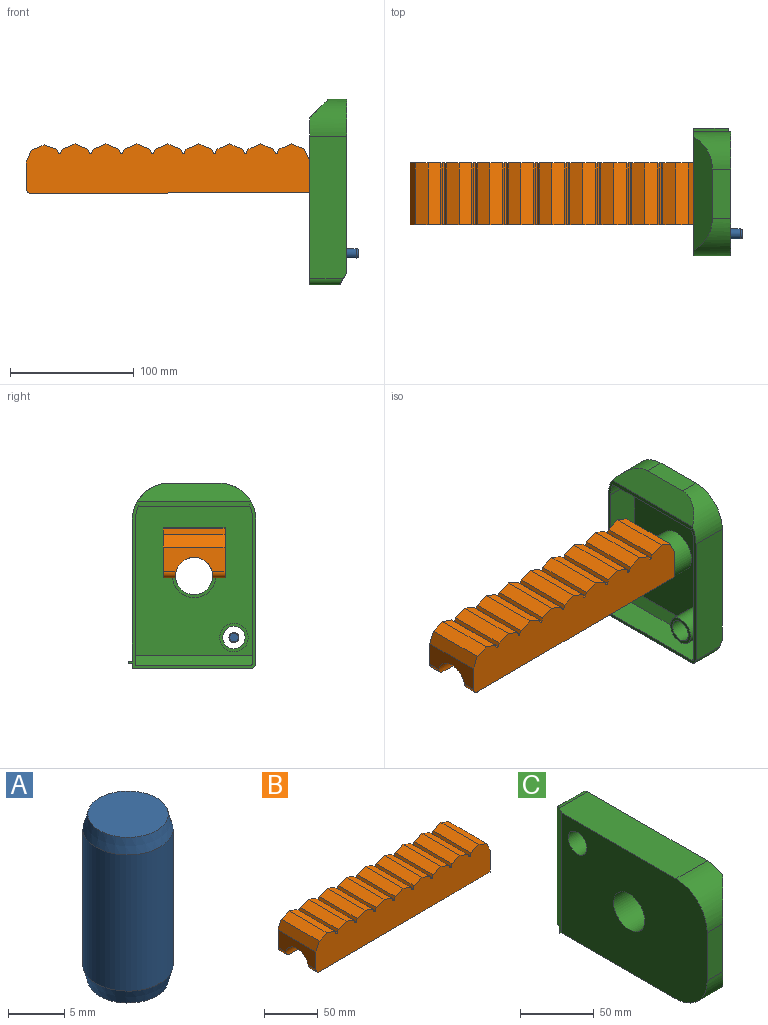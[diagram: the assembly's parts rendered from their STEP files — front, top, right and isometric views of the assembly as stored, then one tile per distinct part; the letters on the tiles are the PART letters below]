
ASSEMBLY  parts=3 mates=2
PART A: 5 faces, bbox 8x8x18 mm
  f0: plane 7.14x7.14mm, normal (0,0,1), area 40.1mm2, adj f1
  f1: cone r=3.57mm half-angle=15deg, axis (0,0,-1), area 39.4mm2, adj f0,f2
  f2: cylinder r=4mm len=14.8mm, axis (0,0,-1), area 372mm2, adj f1,f3
  f3: cone r=4mm half-angle=15deg, axis (0,0,1), area 39.4mm2, adj f2,f4
  f4: plane 7.14x7.14mm, normal (0,0,-1), area 40.1mm2, adj f3
PART B: 53 faces, bbox 229.3x50x40.4 mm
  f0: plane 50x19.96mm, normal (-1,0,0), area 746.4mm2, adj f1,f21,f22,f50,f51,f52
  f1: cylinder r=5mm len=10.39mm, axis (0,1,0), area 79.5mm2, adj f0,f2,f50,f52
  f2: plane 224.25x10.08mm, normal (0.01,0,-1), area 2248.8mm2, adj f1,f23,f50,f52
  f3: plane 224.25x10.08mm, normal (0.01,0,-1), area 2248.8mm2, adj f22,f23,f51,f52
  f4: plane 50x10.36mm, normal (0.38,0,0.92), area 560.4mm2, adj f5,f49,f50,f51
  f5: plane 50x10.36mm, normal (-0.38,0,0.92), area 560.4mm2, adj f4,f6,f50,f51
  f6: plane 50x2.95mm, normal (-0.92,0,0.38), area 159.5mm2, adj f5,f7,f50,f51
  f7: cylinder r=1mm len=50mm, axis (0,1,0), area 117.8mm2, adj f6,f8,f50,f51
  f8: plane 50x2.95mm, normal (0.92,0,0.38), area 159.5mm2, adj f7,f9,f50,f51
  f9: plane 50x10.36mm, normal (0.38,0,0.92), area 560.4mm2, adj f8,f10,f50,f51
  f10: plane 50x10.36mm, normal (-0.38,0,0.92), area 560.4mm2, adj f9,f11,f50,f51
  f11: plane 50x2.95mm, normal (-0.92,0,0.38), area 159.5mm2, adj f10,f12,f50,f51
  f12: cylinder r=1mm len=50mm, axis (0,1,0), area 117.8mm2, adj f11,f13,f50,f51
  f13: plane 50x2.95mm, normal (0.92,0,0.38), area 159.5mm2, adj f12,f14,f50,f51
  f14: plane 50x10.36mm, normal (0.38,0,0.92), area 560.4mm2, adj f13,f15,f50,f51
  f15: plane 50x10.36mm, normal (-0.38,0,0.92), area 560.4mm2, adj f14,f16,f50,f51
  f16: plane 50x2.95mm, normal (-0.92,0,0.38), area 159.5mm2, adj f15,f17,f50,f51
  f17: cylinder r=1mm len=50mm, axis (0,1,0), area 117.8mm2, adj f16,f18,f50,f51
  f18: plane 50x2.95mm, normal (0.92,0,0.38), area 159.5mm2, adj f17,f19,f50,f51
  f19: plane 50x10.36mm, normal (0.32,0,0.95), area 546.7mm2, adj f18,f20,f50,f51
  f20: plane 50x10.36mm, normal (-0.38,0,0.92), area 560.4mm2, adj f19,f21,f50,f51
  f21: plane 50x10.36mm, normal (-0.92,0,0.38), area 560.4mm2, adj f0,f20,f50,f51
  f22: cylinder r=5mm len=10.39mm, axis (0,1,0), area 79.5mm2, adj f0,f3,f51,f52
  f23: plane 50x25mm, normal (1,0,0), area 896.6mm2, adj f2,f3,f24,f50,f51,f52
  f24: plane 50x9.52mm, normal (0.91,0,0.41), area 522.1mm2, adj f23,f25,f50,f51
  f25: plane 50x10.36mm, normal (0.38,0,0.92), area 560.4mm2, adj f24,f26,f50,f51
  f26: plane 50x10.36mm, normal (-0.38,0,0.92), area 560.4mm2, adj f25,f27,f50,f51
  f27: plane 50x2.95mm, normal (-0.92,0,0.38), area 159.5mm2, adj f26,f28,f50,f51
  f28: cylinder r=1mm len=50mm, axis (0,1,0), area 117.8mm2, adj f27,f29,f50,f51
  f29: plane 50x2.95mm, normal (0.92,0,0.38), area 159.5mm2, adj f28,f30,f50,f51
  f30: plane 50x10.36mm, normal (0.38,0,0.92), area 560.4mm2, adj f29,f31,f50,f51
  f31: plane 50x10.36mm, normal (-0.38,0,0.92), area 560.4mm2, adj f30,f32,f50,f51
  f32: plane 50x2.95mm, normal (-0.92,0,0.38), area 159.5mm2, adj f31,f33,f50,f51
  f33: cylinder r=1mm len=50mm, axis (0,1,0), area 117.8mm2, adj f32,f34,f50,f51
  f34: plane 50x2.95mm, normal (0.92,0,0.38), area 159.5mm2, adj f33,f35,f50,f51
  f35: plane 50x10.36mm, normal (0.38,0,0.92), area 560.4mm2, adj f34,f36,f50,f51
  f36: plane 50x10.36mm, normal (-0.38,0,0.92), area 560.4mm2, adj f35,f37,f50,f51
  f37: plane 50x2.95mm, normal (-0.92,0,0.38), area 159.5mm2, adj f36,f38,f50,f51
  f38: cylinder r=1mm len=50mm, axis (0,1,0), area 117.8mm2, adj f37,f39,f50,f51
  f39: plane 50x2.95mm, normal (0.92,0,0.38), area 159.5mm2, adj f38,f40,f50,f51
  f40: plane 50x10.36mm, normal (0.38,0,0.92), area 560.4mm2, adj f39,f41,f50,f51
  f41: plane 50x10.36mm, normal (-0.38,0,0.92), area 560.4mm2, adj f40,f42,f50,f51
  f42: plane 50x2.95mm, normal (-0.92,0,0.38), area 159.5mm2, adj f41,f43,f50,f51
  f43: cylinder r=1mm len=50mm, axis (0,1,0), area 117.8mm2, adj f42,f44,f50,f51
  f44: plane 50x2.95mm, normal (0.92,0,0.38), area 159.5mm2, adj f43,f45,f50,f51
  f45: plane 50x10.36mm, normal (0.38,0,0.92), area 560.4mm2, adj f44,f46,f50,f51
  f46: plane 50x10.36mm, normal (-0.38,0,0.92), area 560.4mm2, adj f45,f47,f50,f51
  f47: plane 50x2.95mm, normal (-0.92,0,0.38), area 159.5mm2, adj f46,f48,f50,f51
  f48: cylinder r=1mm len=50mm, axis (0,1,0), area 117.8mm2, adj f47,f49,f50,f51
  f49: plane 50x2.95mm, normal (0.92,0,0.38), area 159.5mm2, adj f4,f48,f50,f51
  f50: plane 229.29x40.39mm, normal (0,-1,0), area 8357.7mm2, adj f0,f1,f2,f4,f5,f6,f7,f8
  f51: plane 229.29x40.39mm, normal (0,1,0), area 8357.7mm2, adj f0,f3,f4,f5,f6,f7,f8,f9
  f52: cylinder r=15mm len=229.29mm, axis (1,0,0), area 11165.5mm2, adj f0,f1,f2,f3,f22,f23
PART C: 31 faces, bbox 30x150x103.4 mm
  f0: plane 135x103.37mm, normal (1,0,0), area 1231.3mm2, adj f3,f4,f5,f6,f8,f9,f11,f14
  f1: plane 23.1x23.1mm, normal (1,0,0), area 161.8mm2, adj f10,f23
  f2: plane 35x35mm, normal (1,0,0), area 255.3mm2, adj f12,f24
  f3: plane 26.59x3.37mm, normal (0,1,0), area 89.7mm2, adj f0,f4,f11,f17
  f4: plane 26.59x4.09mm, normal (0,0,-1), area 103.9mm2, adj f0,f3,f5,f17
  f5: plane 95x24.23mm, normal (0,1,0), area 2301.5mm2, adj f0,f4,f17,f18
  f6: plane 115x30mm, normal (0,0,1), area 3442.8mm2, adj f0,f13,f14,f17,f18
  f7: plane 40x15mm, normal (0,-1,0), area 600mm2, adj f13,f14,f15,f16
  f8: plane 113.77x30mm, normal (0,0,-1), area 3409mm2, adj f0,f9,f13,f15,f17
  f9: plane 27.82x3.37mm, normal (0,-1,0), area 93.8mm2, adj f0,f8,f11,f17
  f10: cylinder r=9.05mm len=30mm, axis (-1,0,0), area 1705.9mm2, adj f1,f13
  f11: plane 27.82x2.14mm, normal (0,0,-1), area 58.3mm2, adj f0,f3,f9,f17
  f12: cylinder r=15mm len=30mm, axis (-1,0,0), area 2827.4mm2, adj f2,f13
  f13: plane 140x100mm, normal (-1,0,0), area 12649.6mm2, adj f6,f7,f8,f10,f12,f14,f15,f17
  f14: cylinder r=30mm len=30mm, axis (1,0,0), area 1105.5mm2, adj f0,f6,f7,f13,f16
  f15: cylinder r=30mm len=30mm, axis (-1,0,0), area 1105.5mm2, adj f0,f7,f8,f13,f16
  f16: plane 91.96x15mm, normal (0.71,-0.71,0), area 1630.3mm2, adj f0,f7,f14,f15
  f17: plane 103.37x10mm, normal (-0.87,0.5,0), area 1156.9mm2, adj f3,f4,f5,f6,f8,f9,f11,f13
  f18: cylinder r=5mm len=27.11mm, axis (-1,0,0), area 198.5mm2, adj f0,f5,f6,f17
  f19: plane 92.5x22.78mm, normal (0,-1,0), area 2107.4mm2, adj f0,f22,f29,f30
  f20: plane 115x27.5mm, normal (0,0,-1), area 3153.2mm2, adj f0,f25,f26,f29,f30
  f21: plane 40x11.46mm, normal (0,1,0), area 458.6mm2, adj f25,f26,f27,f28
  f22: plane 117.5x27.5mm, normal (0,0,1), area 3212mm2, adj f0,f19,f25,f27,f29
  f23: cylinder r=11.55mm len=27.5mm, axis (-1,0,0), area 1995.7mm2, adj f1,f25
  f24: cylinder r=17.5mm len=35mm, axis (-1,0,0), area 3023.8mm2, adj f2,f25
  f25: plane 136.83x95mm, normal (1,0,0), area 11293.1mm2, adj f20,f21,f22,f23,f24,f26,f27,f29
  f26: cylinder r=27.5mm len=27.5mm, axis (1,0,0), area 860.2mm2, adj f0,f20,f21,f25,f28
  f27: cylinder r=27.5mm len=27.5mm, axis (-1,0,0), area 860.2mm2, adj f0,f21,f22,f25,f28
  f28: plane 89.99x16.04mm, normal (-0.71,0.71,0), area 1721.9mm2, adj f0,f21,f26,f27
  f29: plane 95x8.17mm, normal (0.87,-0.5,0), area 894.7mm2, adj f19,f20,f22,f25,f30
  f30: cylinder r=2.5mm len=24.23mm, axis (-1,0,0), area 91.5mm2, adj f0,f19,f20,f29
PLACE A rot(axis=(0,1,0),90deg) t=(68.88,-18.06,-44.83)mm
PLACE B t=(-48.41,39.13,-5.71)mm
PLACE C rot(axis=(0,-0.71,0.71),180deg) t=(68.88,14.13,4.91)mm
MATE fastened A.f1 <-> C.f10  axis (1,0,0) through (68.88,-18.06,-44.83)mm
MATE fastened C.f12 <-> B.f52  axis (-1,0,0) through (38.88,14.13,4.91)mm
